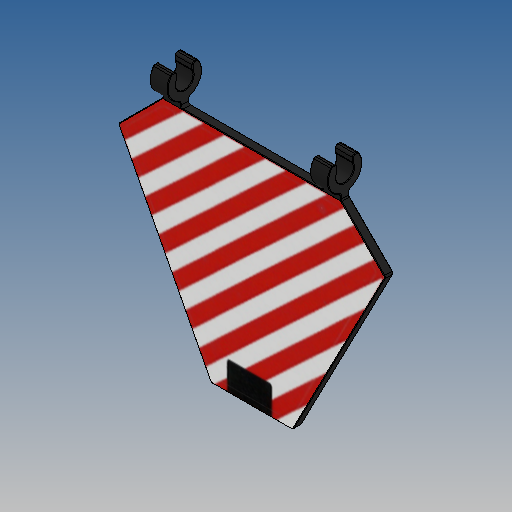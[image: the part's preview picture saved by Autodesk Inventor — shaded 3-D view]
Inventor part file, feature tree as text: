
AUTODESK INVENTOR PART (.ipt)
format: ipt  version: 2025.1 (Build 291241000, 241)  size: 969,216 bytes
history: native  units: mm
features: sketch x7, extrude x5, other x4, fillet x2, mirror x1
ambient origin geometry x8: Origin, YZ Plane, XZ Plane, XY Plane, X Axis, Y Axis, Z Axis, Center Point
bodies: Volumenkörper1 (feature_tree)
feature tree (19):
  extrude  "Extrusion1"  Depth=40.0mm
  extrude  "Extrusion2"  Depth=4.0mm
  fillet  "Rundung1"  [1 undecoded]
  extrude  "Extrusion3"  Depth=1.5mm
  fillet  "Rundung2"  Radius=1.5mm
  mirror  "Spiegeln1"
  extrude  "Extrusion4"  Depth=3.2mm
  extrude  "Extrusion5"  Depth=2.8mm
  other  "Aufkleber1"
  other  "Aufkleber2"
  sketch  "Skizze1"  dims[d0=40.0mm d1=24.0mm]
  sketch  "Skizze2"  dims[d2=16.0mm d3=4.0mm d5=45.0deg]
  sketch  "Skizze3"  dims[d6=4.799655mm d7=7.341854mm d8=1.5mm d9=0.0mm]
  sketch  "Skizze4"  dims[d10=3.2mm d11=6.2mm]
  other  "Bild1"
  sketch  "Skizze5"  dims[d12=6.0mm d13=2.8mm]
  sketch  "Skizze6"  dims[d14=16.0mm d15=0.0mm]
  sketch  "Skizze7"  dims[d16=0.4mm d17=0.1mm d18=4.0mm d19=3.2mm d20=0.0mm d21=0.0mm d22=0.1mm d23=0.4mm d30=0.01mm d31=0.0mm d32=0.01mm d33=0.0mm d40=50.0mm d46=1.5mm d51=25.5mm d57=2.0mm d58=50.0mm d61=24.5mm]
  other  "Bild2"
note: 1 required parameter value undecoded (feature->parameter linkage not recoverable at this tier; creation-order binding heuristic only, values carry confidence <= 0.55)
